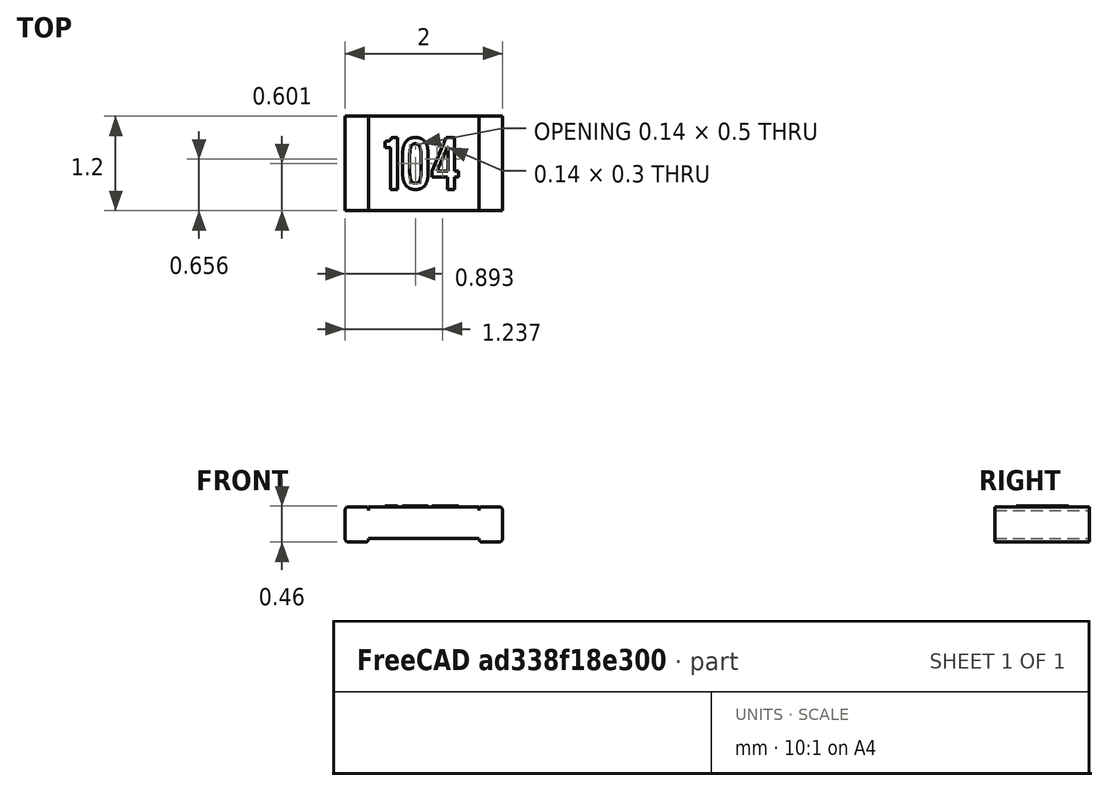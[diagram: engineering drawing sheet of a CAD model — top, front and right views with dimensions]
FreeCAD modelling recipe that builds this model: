
FCSTD DOCUMENT  (FreeCAD 0.19R16945 (Git))
Label: Parametric Part Family
License: All rights reserved
LicenseURL: http://en.wikipedia.org/wiki/All_rights_reserved
objects: Part::Feature×1, Part::Part2DObjectPython×1, Part::Extrusion×1
note: 3 computed .brp shape members not serialized (recipe doc carries the construction recipe); baked Part::Feature solids carry a one-line shape summary decoded from their .brp

FEATURE [Part::Feature] Part__Feature  label="R_0805_2012Metric"
  shape: bbox 2 x 1.2 x 0.45 mm, 26 faces (baked)
FEATURE [Part::Part2DObjectPython] ShapeString  # Draft 2D object (typed FeaturePython)
  AttachmentOffset = pos=(-0.19,-0.27,0) rot=(0,0,1;3.14159rad)
  FontFile = <userpath>/Desktop/GitHub/freecad-projects/00-fonts/coolvetica condensed rg.ttf
  MapMode = 6
  Placement = pos=(-0.51,-0.33,0.45) rot=(0,0,1;0rad)
  Size = 0.4
  String = 104
  Support = -> [Part__Feature]
  Tracking = 0
  expr: AttachmentOffset.Base.x = -0.7 + 0.46 + 0.05
  expr: AttachmentOffset.Base.y = -0.6 + 0.33
FEATURE [Part::Extrusion] Extrude
  Base = -> ShapeString
  Dir = (0,0,1)
  DirMode = 2
  FaceMakerClass = Part::FaceMakerBullseye
  LengthFwd = 0.01
  LengthRev = 0
  Solid = false
  Symmetric = false
